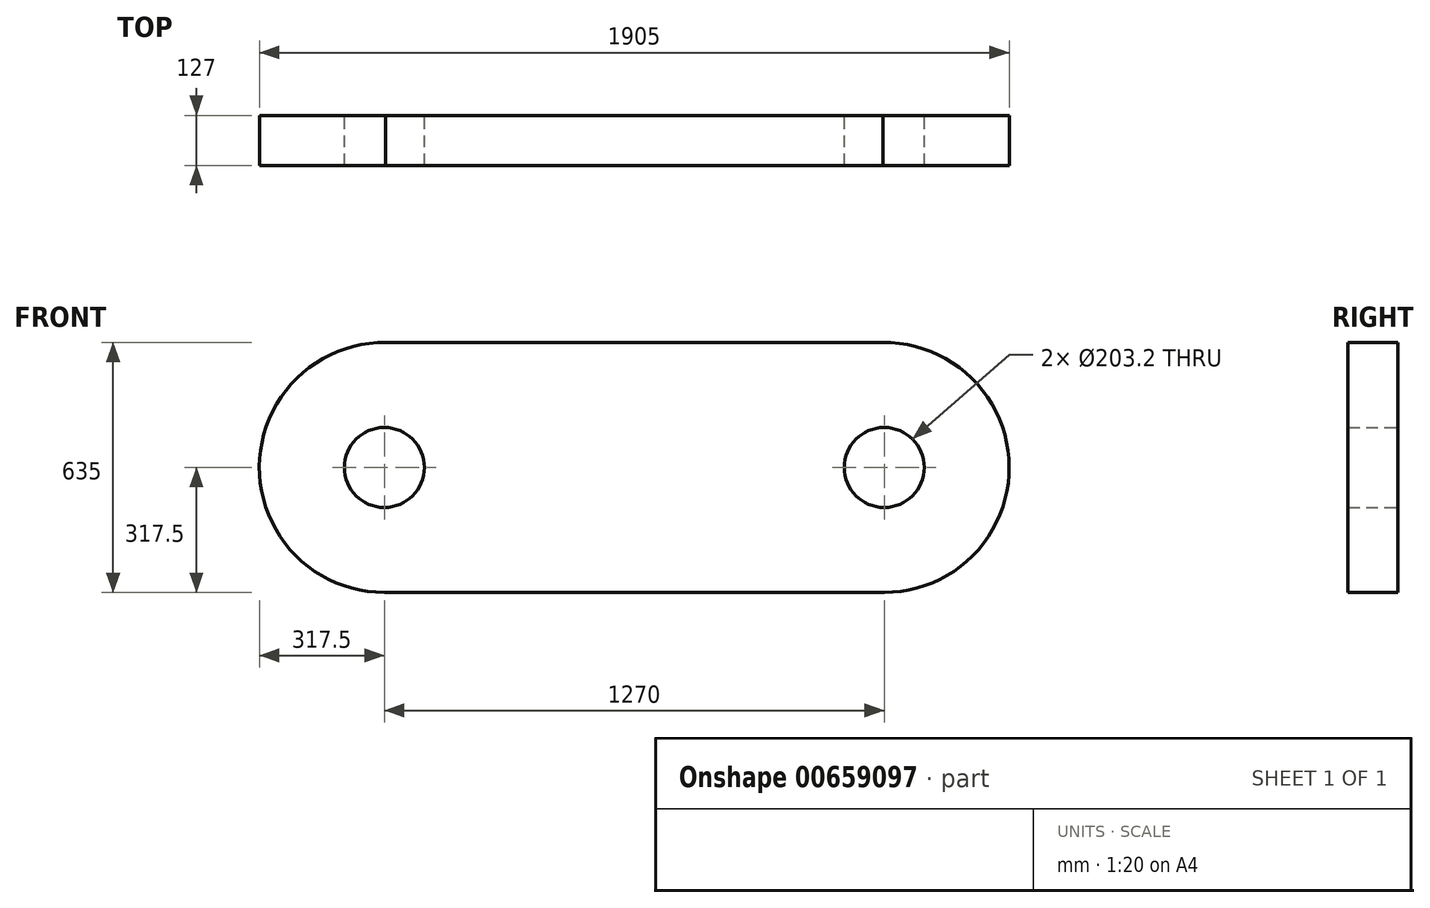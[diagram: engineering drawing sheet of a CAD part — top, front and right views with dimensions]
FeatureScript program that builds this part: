
annotation { "Feature Type Name" : "Feature", "Feature Type Description" : "" }
export const myFeature = defineFeature(function(context is Context, id is Id, definition is map)
    precondition{}
    {
        {
            var Q0;
            Q0=qCreatedBy(makeId("Front.planeOp"),FACE);
            var sketch = newSketch(context, id + "F0", { "sketchPlane" : qUnion([Q0])});
            skArc(sketch, "E0", {"start": v(-631.2, 317.48) * mm, "mid": v(-952.5, 1.9) * mm, "end": v(-635, -317.5) * mm});
            skLineSegment(sketch, "E1", {"start": v(-631.2, 317.48) * mm, "end": v(0, 317.48) * mm});
            skLineSegment(sketch, "E2", {"start": v(-635, -317.5) * mm, "end": v(0, -317.5) * mm});
            skCircle(sketch, "E3", {"center": v(-635, 0) * mm, "radius": 101.6 * mm});
            skLineSegment(sketch, "E4.MirrorCS", {"start": v(631.2, 317.48) * mm, "end": v(0, 317.48) * mm});
            skArc(sketch, "E5.MirrorCS", {"start": v(631.2, 317.48) * mm, "mid": v(952.5, 1.9) * mm, "end": v(635, -317.5) * mm});
            skCircle(sketch, "E6.MirrorC", {"center": v(635, 0) * mm, "radius": 101.6 * mm});
            skLineSegment(sketch, "E7.MirrorCS", {"start": v(635, -317.5) * mm, "end": v(0, -317.5) * mm});
            skSolve(sketch);
        }
        {
            var Q0;
            Q0 = qSketchRegion(id + "F0", true);
            extrude(context, id + "F1", {"entities" : qUnion([Q0]), "depth" : 127 * mm, "offsetDistance" : 25.4 * mm});
        }
    });
